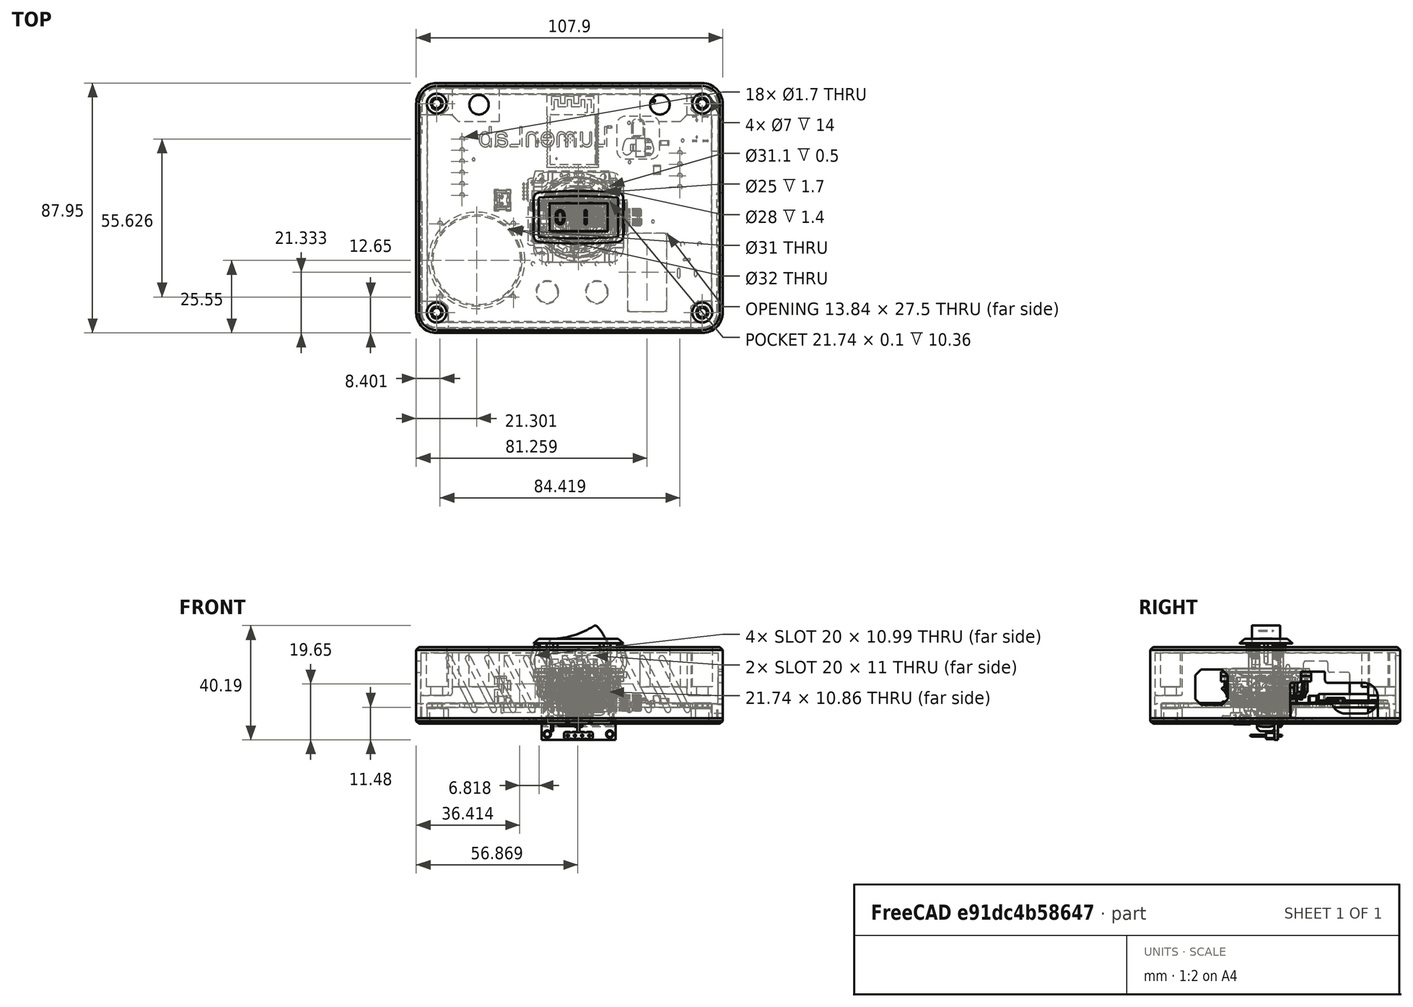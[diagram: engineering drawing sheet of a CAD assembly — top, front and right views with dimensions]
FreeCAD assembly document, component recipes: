
FREECAD ASSEMBLY — COMPONENT RECIPES ("lumenlab-enclosure")

This assembly document has 7 components, labeled P0..P6 below (a component is one placed body or linked part). 6 of them carry a construction recipe — the FreeCAD feature program that regenerates the part from scratch, quoted from this document or its linked companion documents; the rest are supplied as boundary geometry only. No exploded tour is included for this assembly.
COMPONENT P0 — geometry summary ("lumenlab-pcb001"; no construction recipe available for this part):
  bounding box: 106.5 x 80.0 x 42.6 mm
  tessellated surface: 422,423 triangles
  volume: 30416 mm^3 (8% of its bounding box)
COMPONENT P1 — recipe-attached ("lid", modeled in this document).
Construction recipe (the document's own serialized feature program — sketch geometry with constraints, then the solid features built on it; lengths are millimeters unless a unit is written):

FEATURE [PartDesign::SubShapeBinder] Binder
  BindCopyOnChange = 0
  BindMode = 0
  ClaimChildren = false
  Context = -> Body [Binder.]
  Fuse = false
  MakeFace = true
  OffsetFill = false
  OffsetIntersection = false
  OffsetJoinType = 0
  OffsetOpenResult = false
  PartialLoad = false
  Refine = true
  Relative = true
  Support = -> [Board_aaa008]
  _Version = 2
FEATURE [Sketcher::SketchObject] Sketch
  ArcFitTolerance = 1e-06
  AttachmentOffset = pos=(0,0,3.75) rot=(0,0,1;0rad)
  AttachmentSupport = -> [Binder]
  ExternalGeometry = -> [Binder]
  ExternalTypes = [0]
  FullyConstrained = true
  MakeInternals = false
  MapMode = 5
  Placement = pos=(0,0,-5.3502) rot=(1,0,0;3.14159rad)
  _ExternalGeoVersion = 0
  sketch-geometry (10):
    g0: LineSegment StartX=-57.1492 StartY=33.5464 StartZ=0 EndX=-57.1492 EndY=-39.9989 EndZ=0
    g1: LineSegment StartX=-49.9485 StartY=-47.1996 StartZ=0 EndX=43.5501 EndY=-47.1996 EndZ=0
    g2: LineSegment StartX=50.7508 StartY=-39.9989 StartZ=0 EndX=50.7508 EndY=33.5464 EndZ=0
    g3: LineSegment StartX=43.5501 StartY=40.7472 StartZ=0 EndX=-49.9485 EndY=40.7472 EndZ=0
    g4: ArcOfCircle CenterX=-49.9485 CenterY=33.5464 CenterZ=0 NormalX=0 NormalY=0 NormalZ=1 AngleXU=0 Radius=7.20071 StartAngle=1.5708 EndAngle=3.14159
    g5: ArcOfCircle CenterX=-49.9485 CenterY=-39.9989 CenterZ=0 NormalX=0 NormalY=0 NormalZ=1 AngleXU=0 Radius=7.20071 StartAngle=3.14159 EndAngle=4.71239
    g6: ArcOfCircle CenterX=43.5501 CenterY=-39.9989 CenterZ=0 NormalX=0 NormalY=0 NormalZ=1 AngleXU=0 Radius=7.20071 StartAngle=4.71239 EndAngle=6.28319
    g7: ArcOfCircle CenterX=43.5501 CenterY=33.5464 CenterZ=0 NormalX=0 NormalY=0 NormalZ=1 AngleXU=0 Radius=7.20071 StartAngle=1e-16 EndAngle=1.5708
    g8: GeomPoint [constr] X=-57.1492 Y=40.7472 Z=0
    g9: GeomPoint [constr] X=50.7508 Y=-47.1996 Z=0
  constraints (23):
    c: Tangent(g0,g4) = -1.5708
    c: Tangent(g0,g5) = -1.5708
    c: Tangent(g1,g5) = -1.5708
    c: Tangent(g1,g6) = -1.5708
    c: Tangent(g2,g6) = -1.5708
    c: Tangent(g2,g7) = -1.5708
    c: Tangent(g3,g7) = -1.5708
    c: Tangent(g3,g4) = -1.5708
    c: Vertical(g0)
    c: Vertical(g2)
    c: Horizontal(g1)
    c: Horizontal(g3)
    c: Equal(g4,g5)
    c: Equal(g5,g6)
    c: Equal(g6,g7)
    c: PointOnObject(g8,g0)
    c: PointOnObject(g8,g3)
    c: PointOnObject(g9,g1)
    c: PointOnObject(g9,g2)
    c: DistanceX(g0,g-5) = 4  'enclosure-width'
    c: Coincident(g4,g-4)
    c: Distance(g-7,g2) = 4
    c: Distance(g-9,g1) = 4
FEATURE [PartDesign::Pad] Pad
  Direction = (0,0,-1)
  Length = 2
  Length2 = 10
  Profile = -> Sketch
  ReferenceAxis = -> Sketch [N_Axis]
  Refine = true
  SideType = 0
  Suppressed = false
  Type = 0
  Type2 = 0
FEATURE [Sketcher::SketchObject] Sketch001
  ArcFitTolerance = 1e-06
  AttachmentSupport = -> [Pad]
  ExternalGeometry = -> [Binder]
  ExternalTypes = [0]
  FullyConstrained = true
  MakeInternals = false
  MapMode = 5
  Placement = pos=(0,0,-5.3502) rot=(0,0,1;0rad)
  _ExternalGeoVersion = 0
  sketch-geometry (20):
    g0: LineSegment StartX=-55.15 StartY=39.9996 StartZ=0 EndX=-55.15 EndY=-33.5498 EndZ=0
    g1: LineSegment StartX=-49.95 StartY=-38.7498 StartZ=0 EndX=43.551 EndY=-38.7498 EndZ=0
    g2: LineSegment StartX=48.751 StartY=-33.5498 StartZ=0 EndX=48.751 EndY=39.9996 EndZ=0
    g3: LineSegment StartX=43.551 StartY=45.1996 StartZ=0 EndX=-49.95 EndY=45.1996 EndZ=0
    g4: ArcOfCircle CenterX=-49.95 CenterY=39.9996 CenterZ=0 NormalX=0 NormalY=0 NormalZ=1 AngleXU=0 Radius=5.19999 StartAngle=1.5708 EndAngle=3.14159
    g5: ArcOfCircle CenterX=-49.95 CenterY=-33.5498 CenterZ=0 NormalX=0 NormalY=0 NormalZ=1 AngleXU=0 Radius=5.19999 StartAngle=3.14159 EndAngle=4.71239
    g6: ArcOfCircle CenterX=43.551 CenterY=-33.5498 CenterZ=0 NormalX=0 NormalY=0 NormalZ=1 AngleXU=0 Radius=5.19999 StartAngle=4.71239 EndAngle=6.28319
    g7: ArcOfCircle CenterX=43.551 CenterY=39.9996 CenterZ=0 NormalX=0 NormalY=0 NormalZ=1 AngleXU=0 Radius=5.19999 StartAngle=5e-16 EndAngle=1.5708
    g8: GeomPoint [constr] X=-55.15 Y=45.1996 Z=0
    g9: GeomPoint [constr] X=48.751 Y=-38.7498 Z=0
    g10: LineSegment StartX=-53.35 StartY=39.9996 StartZ=0 EndX=-53.35 EndY=-33.5498 EndZ=0
    g11: LineSegment StartX=-49.95 StartY=-36.9498 StartZ=0 EndX=43.551 EndY=-36.9498 EndZ=0
    g12: LineSegment StartX=46.951 StartY=-33.5498 StartZ=0 EndX=46.951 EndY=39.9996 EndZ=0
    g13: LineSegment StartX=43.551 StartY=43.3996 StartZ=0 EndX=-49.95 EndY=43.3996 EndZ=0
    g14: ArcOfCircle CenterX=-49.95 CenterY=39.9996 CenterZ=0 NormalX=0 NormalY=0 NormalZ=1 AngleXU=0 Radius=3.39999 StartAngle=1.5708 EndAngle=3.14159
    g15: ArcOfCircle CenterX=-49.95 CenterY=-33.5498 CenterZ=0 NormalX=0 NormalY=0 NormalZ=1 AngleXU=0 Radius=3.39999 StartAngle=3.14159 EndAngle=4.71239
    g16: ArcOfCircle CenterX=43.551 CenterY=-33.5498 CenterZ=0 NormalX=0 NormalY=0 NormalZ=1 AngleXU=0 Radius=3.39999 StartAngle=4.71239 EndAngle=6.28319
    g17: ArcOfCircle CenterX=43.551 CenterY=39.9996 CenterZ=0 NormalX=0 NormalY=0 NormalZ=1 AngleXU=0 Radius=3.39999 StartAngle=0 EndAngle=1.5708
    g18: GeomPoint [constr] X=-53.35 Y=43.3996 Z=0
    g19: GeomPoint [constr] X=46.951 Y=-36.9498 Z=0
  constraints (46):
    c: Tangent(g0,g4) = -1.5708
    c: Tangent(g0,g5) = -1.5708
    c: Tangent(g1,g5) = -1.5708
    c: Tangent(g1,g6) = -1.5708
    c: Tangent(g2,g6) = -1.5708
    c: Tangent(g2,g7) = -1.5708
    c: Tangent(g3,g7) = -1.5708
    c: Tangent(g3,g4) = -1.5708
    c: Vertical(g0)
    c: Vertical(g2)
    c: Horizontal(g1)
    c: Horizontal(g3)
    c: Equal(g4,g5)
    c: Equal(g5,g6)
    c: Equal(g6,g7)
    c: PointOnObject(g8,g0)
    c: PointOnObject(g8,g3)
    c: PointOnObject(g9,g1)
    c: PointOnObject(g9,g2)
    c: DistanceX(g0,g-5) = 2
    c: Coincident(g4,g-4)
    c: DistanceX(g-7,g2) = 2
    c: DistanceY(g1,g-9) = 2
    c: Tangent(g10,g14) = -1.5708
    c: Tangent(g10,g15) = -1.5708
    c: Tangent(g11,g15) = -1.5708
    c: Tangent(g11,g16) = -1.5708
    c: Tangent(g12,g16) = -1.5708
    c: Tangent(g12,g17) = -1.5708
    c: Tangent(g13,g17) = -1.5708
    c: Tangent(g13,g14) = -1.5708
    c: Vertical(g10)
    c: Vertical(g12)
    c: Horizontal(g11)
    c: Horizontal(g13)
    c: Equal(g14,g15)
    c: Equal(g15,g16)
    c: Equal(g16,g17)
    c: PointOnObject(g18,g10)
    c: PointOnObject(g18,g13)
    c: PointOnObject(g19,g11)
    c: PointOnObject(g19,g12)
    c: DistanceX(g10,g-5) = 0.2
    c: DistanceX(g-7,g12) = 0.2
    c: DistanceY(g11,g-9) = 0.2
    c: Coincident(g14,g4)
FEATURE [PartDesign::Pad] Pad001
  BaseFeature = -> Pad
  Direction = (0,0,1)
  Length = 5
  Length2 = 10
  Profile = -> Sketch001
  ReferenceAxis = -> Sketch001 [N_Axis]
  Refine = true
  SideType = 0
  Suppressed = false
  Type = 0
  Type2 = 0
FEATURE [Sketcher::SketchObject] Sketch002
  ArcFitTolerance = 1e-06
  ExternalGeometry = -> [Binder,Pad001]
  ExternalTypes = [0]
  FullyConstrained = true
  MakeInternals = false
  MapMode = 5
  Placement = pos=(0,0,-2) rot=(1,0,0;3.14159rad)
  _ExternalGeoVersion = 0
  sketch-geometry (10):
    g0: LineSegment StartX=-53.1492 StartY=29.5498 StartZ=0 EndX=-53.35 EndY=29.5498 EndZ=0
    g1: LineSegment StartX=-45.95 StartY=36.7473 StartZ=0 EndX=-45.95 EndY=36.9498 EndZ=0
    g2: LineSegment StartX=-45.95 StartY=36.9498 StartZ=0 EndX=-49.95 EndY=36.9498 EndZ=0
    g3: LineSegment StartX=-53.35 StartY=29.5498 StartZ=0 EndX=-53.35 EndY=33.5498 EndZ=0
    g4: ArcOfCircle CenterX=-49.95 CenterY=33.5498 CenterZ=0 NormalX=0 NormalY=0 NormalZ=1 AngleXU=0 Radius=3.39999 StartAngle=1.5708 EndAngle=3.14159
    g5: LineSegment StartX=-53.1492 StartY=29.5498 StartZ=0 EndX=-48.6466 EndY=29.5498 EndZ=0
    g6: ArcOfCircle CenterX=-48.6466 CenterY=30.4451 CenterZ=0 NormalX=0 NormalY=0 NormalZ=1 AngleXU=0 Radius=0.895293 StartAngle=4.71239 EndAngle=5.38086
    g7: LineSegment StartX=-48.0918 StartY=29.7425 StartZ=0 EndX=-46.138 EndY=31.2855 EndZ=0
    g8: ArcOfCircle CenterX=-46.4444 CenterY=31.6735 CenterZ=0 NormalX=0 NormalY=0 NormalZ=1 AngleXU=0 Radius=0.494368 StartAngle=5.38086 EndAngle=6.28319
    g9: LineSegment StartX=-45.95 StartY=31.6735 StartZ=0 EndX=-45.95 EndY=36.7473 EndZ=0
  constraints (24):
    c: PointOnObject(g0,g-8)
    c: Horizontal(g0)
    c: PointOnObject(g1,g-7)
    c: Vertical(g1)
    c: Coincident(g2,g1)
    c: Coincident(g2,g-9)
    c: Coincident(g3,g0)
    c: Coincident(g3,g-9)
    c: Coincident(g4,g2)
    c: Coincident(g4,g3)
    c: PointOnObject(g0,g-10)
    c: PointOnObject(g1,g-11)
    c: DistanceY(g3,g3) = 4
    c: DistanceX(g2,g2) = 4
    c: Equal(g4,g-9)
    c: Coincident(g0,g5)
    c: Tangent(g5,g6) = -1.5708
    c: Tangent(g6,g7) = -1.5708
    c: Tangent(g7,g8) = -1.5708
    c: Tangent(g8,g9) = -1.5708
    c: Vertical(g9)
    c: Coincident(g9,g1)
    c: Horizontal(g5)
    c: Block(g7)
FEATURE [PartDesign::Pad] Pad002
  BaseFeature = -> Pad001
  Direction = (0,-1e-16,-1)
  Length = 10
  Length2 = 10
  Profile = -> Sketch002
  ReferenceAxis = -> Sketch002 [N_Axis]
  Refine = true
  SideType = 0
  Suppressed = false
  Type = 2
  Type2 = 0
FEATURE [PartDesign::Plane] DatumPlane
  AttachmentOffset = pos=(0,0,0) rot=(1,0,0;1.5708rad)
  AttachmentSupport = -> [Pad002]
  Length = 122.591
  MapMode = 45
  Placement = pos=(-3.1995,3.22491,-2.8502) rot=(1,0,0;1.5708rad)
  ResizeMode = 0
  Width = 64.6902
  expr: .AttachmentOffset.Rotation.Pitch = 0
FEATURE [PartDesign::Plane] DatumPlane001
  AttachmentOffset = pos=(0,0,0) rot=(1,0,0;1.5708rad)
  AttachmentSupport = -> [Pad002]
  Length = 101.209
  MapMode = 45
  Placement = pos=(-3.1995,3.22491,-2.8502) rot=(0.57735,0.57735,0.57735;2.0944rad)
  ResizeMode = 0
  Width = 63.2625
FEATURE [PartDesign::Line] DatumLine
  AttacherType = Attacher::AttachEngineLine
  AttachmentSupport = -> [DatumPlane001,DatumPlane]
  Length = 20
  MapMode = 30
  Placement = pos=(-3.1995,3.22491,-2.8502) rot=(0,1,0;3.14159rad)
  ResizeMode = 0
FEATURE [PartDesign::Mirrored] Mirrored
  BaseFeature = -> Pad002
  MirrorPlane = -> DatumPlane
  Originals = -> [Pad002]
  Refine = true
  Suppressed = false
  TransformMode = 0
FEATURE [PartDesign::Mirrored] Mirrored001
  BaseFeature = -> Mirrored
  MirrorPlane = -> DatumPlane001
  Originals = -> [Pad002]
  Refine = true
  Suppressed = false
  TransformMode = 0
FEATURE [PartDesign::PolarPattern] PolarPattern
  Angle = 360
  Axis = -> DatumLine
  BaseFeature = -> Mirrored001
  Mode = 0
  Occurrences = 2
  Offset = 120
  Originals = -> [Pad002]
  Refine = true
  Reversed = true
  SpacingPattern = [0]
  Spacings = [-1]
  Suppressed = false
  TransformMode = 0
FEATURE [Sketcher::SketchObject] Sketch003
  ArcFitTolerance = 1e-06
  AttachmentSupport = -> [PolarPattern]
  ExternalTypes = [0]
  FullyConstrained = true
  MakeInternals = false
  MapMode = 5
  Placement = pos=(0,0,-2) rot=(0,0,1;0rad)
  _ExternalGeoVersion = 0
  sketch-geometry (1):
    g0: Circle CenterX=-49.95 CenterY=-33.5498 CenterZ=0 NormalX=0 NormalY=0 NormalZ=1 AngleXU=0 Radius=2.425
  constraints (2):
    c: Coincident(g0,g-3)
    c: Diameter(g0) = 4.85
FEATURE [PartDesign::Pocket] Pocket
  BaseFeature = -> PolarPattern
  Direction = (0,0,-1)
  Length = 4.35
  Length2 = 5
  Profile = -> Sketch003
  ReferenceAxis = -> Sketch003 [N_Axis]
  Refine = true
  SideType = 0
  Suppressed = false
  Type = 0
  Type2 = 0
FEATURE [PartDesign::Mirrored] Mirrored002
  BaseFeature = -> Pocket
  MirrorPlane = -> DatumPlane
  Originals = -> [Pocket]
  Refine = true
  Suppressed = false
  TransformMode = 0
FEATURE [PartDesign::Mirrored] Mirrored003
  BaseFeature = -> Mirrored002
  MirrorPlane = -> DatumPlane001
  Originals = -> [Pocket]
  Refine = true
  Suppressed = false
  TransformMode = 0
FEATURE [PartDesign::PolarPattern] PolarPattern001
  Angle = 360
  Axis = -> DatumLine
  BaseFeature = -> Mirrored003
  Mode = 0
  Occurrences = 2
  Offset = 120
  Originals = -> [Pocket]
  Refine = true
  SpacingPattern = [0]
  Spacings = [-1]
  Suppressed = false
  TransformMode = 0
FEATURE [Sketcher::SketchObject] Sketch004
  ArcFitTolerance = 1e-06
  AttachmentSupport = -> [Pad]
  ExternalTypes = [0]
  FullyConstrained = true
  MakeInternals = false
  MapMode = 5
  Placement = pos=(0,0,-5.3502) rot=(0,0,1;0rad)
  _ExternalGeoVersion = 0
  sketch-geometry (16):
    g0: LineSegment StartX=17.1876 StartY=-6.3741 StartZ=0 EndX=17.1876 EndY=-32.4599 EndZ=0
    g1: LineSegment StartX=17.8947 StartY=-33.167 StartZ=0 EndX=30.3239 EndY=-33.167 EndZ=0
    g2: LineSegment StartX=31.031 StartY=-32.4599 StartZ=0 EndX=31.031 EndY=-6.3741 EndZ=0
    g3: LineSegment StartX=30.3239 StartY=-5.66699 StartZ=0 EndX=17.8947 EndY=-5.66699 EndZ=0
    g4: ArcOfCircle [constr] CenterX=17.8947 CenterY=-6.3741 CenterZ=0 NormalX=0 NormalY=0 NormalZ=1 AngleXU=0 Radius=0.707107 StartAngle=1.5708 EndAngle=3.14159
    g5: GeomPoint [constr] X=17.1876 Y=-5.66699 Z=0
    g6: LineSegment StartX=17.8947 StartY=-5.66699 StartZ=0 EndX=17.1876 EndY=-6.3741 EndZ=0
    g7: ArcOfCircle [constr] CenterX=30.3239 CenterY=-6.3741 CenterZ=0 NormalX=0 NormalY=0 NormalZ=1 AngleXU=0 Radius=0.707107 StartAngle=-1.8e-15 EndAngle=1.5708
    g8: GeomPoint [constr] X=31.031 Y=-5.66699 Z=0
    g9: LineSegment StartX=31.031 StartY=-6.3741 StartZ=0 EndX=30.3239 EndY=-5.66699 EndZ=0
    g10: ArcOfCircle [constr] CenterX=30.3239 CenterY=-32.4599 CenterZ=0 NormalX=0 NormalY=0 NormalZ=1 AngleXU=0 Radius=0.707107 StartAngle=4.71239 EndAngle=6.28319
    g11: GeomPoint [constr] X=31.031 Y=-33.167 Z=0
    g12: LineSegment StartX=30.3239 StartY=-33.167 StartZ=0 EndX=31.031 EndY=-32.4599 EndZ=0
    g13: ArcOfCircle [constr] CenterX=17.8947 CenterY=-32.4599 CenterZ=0 NormalX=0 NormalY=0 NormalZ=1 AngleXU=0 Radius=0.707107 StartAngle=3.14159 EndAngle=4.71239
    g14: GeomPoint [constr] X=17.1876 Y=-33.167 Z=0
    g15: LineSegment StartX=17.1876 StartY=-32.4599 StartZ=0 EndX=17.8947 EndY=-33.167 EndZ=0
  constraints (36):
    c: Vertical(g0)
    c: Vertical(g2)
    c: Horizontal(g1)
    c: Distance(g14,g5) = 27.5
    c: Tangent(g0,g4) = -1.5708
    c: Tangent(g3,g4) = -1.5708
    c: Coincident(g6,g0)
    c: Coincident(g6,g3)
    c: Tangent(g2,g7) = -1.5708
    c: Tangent(g3,g7) = -1.5708
    c: Coincident(g9,g2)
    c: Coincident(g9,g3)
    c: PointOnObject(g11,g1)
    c: PointOnObject(g11,g2)
    c: Tangent(g1,g10) = -1.5708
    c: Tangent(g2,g10) = -1.5708
    c: Coincident(g12,g1)
    c: Coincident(g12,g2)
    c: PointOnObject(g14,g0)
    c: PointOnObject(g14,g1)
    c: Tangent(g0,g13) = -1.5708
    c: Tangent(g1,g13) = -1.5708
    c: Coincident(g15,g0)
    c: Coincident(g15,g1)
    c: DistanceX(g5,g-6) = 0.25
    c: Vertical(g5,g0)
    c: Horizontal(g3,g5)
    c: Horizontal(g-3,g3)
    c: Horizontal(g3)
    c: DistanceX(g8,g-6) = -0.25
    c: Vertical(g8,g2)
    c: Horizontal(g8,g3)
    c: Equal(g15,g12)
    c: Distance(g15,g15) = 1
    c: Equal(g15,g6)
    c: Equal(g15,g9)
FEATURE [PartDesign::Pocket] Pocket001
  BaseFeature = -> PolarPattern001
  Direction = (0,0,-1)
  Length = 5
  Length2 = 5
  Profile = -> Sketch004
  ReferenceAxis = -> Sketch004 [N_Axis]
  Refine = true
  SideType = 0
  Suppressed = false
  Type = 1
  Type2 = 0
FEATURE [Sketcher::SketchObject] Sketch005
  ArcFitTolerance = 1e-06
  AttachmentSupport = -> [Pocket001]
  ExternalGeometry = -> [Binder]
  ExternalTypes = [0]
  FullyConstrained = true
  MakeInternals = false
  MapMode = 5
  Placement = pos=(0,0,-5.3502) rot=(0,0,1;0rad)
  _ExternalGeoVersion = 0
  sketch-geometry (2):
    g0: Circle CenterX=-11.0304 CenterY=-26.366 CenterZ=0 NormalX=0 NormalY=0 NormalZ=1 AngleXU=0 Radius=4
    g1: Circle CenterX=6.40289 CenterY=-26.366 CenterZ=0 NormalX=0 NormalY=0 NormalZ=1 AngleXU=0 Radius=4
  constraints (4):
    c: Diameter(g1) = 8
    c: Diameter(g0) = 8
    c: Coincident(g0,g-3)
    c: Coincident(g1,g-4)
FEATURE [PartDesign::Pocket] Pocket002
  BaseFeature = -> Pocket001
  Direction = (0,0,-1)
  Length = 5
  Length2 = 5
  Profile = -> Sketch005
  ReferenceAxis = -> Sketch005 [N_Axis]
  Refine = true
  SideType = 0
  Suppressed = false
  Type = 1
  Type2 = 0
FEATURE [Sketcher::SketchObject] Sketch006
  ArcFitTolerance = 1e-06
  AttachmentSupport = -> [Pocket002]
  ExternalGeometry = -> [Binder]
  ExternalTypes = [0]
  FullyConstrained = true
  MakeInternals = false
  MapMode = 5
  Placement = pos=(0,0,-7.3502) rot=(1,0,0;3.14159rad)
  _ExternalGeoVersion = 0
  sketch-geometry (7):
    g0: GeomPoint [constr] X=-14.1384 Y=2.33766 Z=0
    g1: LineSegment StartX=-16.2684 StartY=8.33766 StartZ=0 EndX=-16.2684 EndY=-12.1623 EndZ=0
    g2: LineSegment StartX=-16.2684 StartY=-12.1623 StartZ=0 EndX=11.7316 EndY=-12.1623 EndZ=0
    g3: LineSegment StartX=11.7316 StartY=-12.1623 StartZ=0 EndX=11.7316 EndY=8.33766 EndZ=0
    g4: LineSegment StartX=11.7316 StartY=8.33766 StartZ=0 EndX=-16.2684 EndY=8.33766 EndZ=0
    g5: LineSegment [constr] StartX=-14.1384 StartY=2.33766 StartZ=0 EndX=-16.2684 EndY=8.33766 EndZ=0
    g6: LineSegment [constr] StartX=9.60158 StartY=2.33766 StartZ=0 EndX=11.7316 EndY=8.33766 EndZ=0
  constraints (17):
    c: Coincident(g0,g-4)
    c: Coincident(g1,g2)
    c: Coincident(g2,g3)
    c: Coincident(g3,g4)
    c: Coincident(g4,g1)
    c: Vertical(g1)
    c: Vertical(g3)
    c: Horizontal(g2)
    c: Horizontal(g4)
    c: Distance(g1,g3) = 28
    c: Distance(g2,g4) = 20.5
    c: Coincident(g5,g0)
    c: Coincident(g5,g1)
    c: Coincident(g6,g3)
    c: Coincident(g-3,g6)
    c: Equal(g5,g6)
    c: Distance(g2,g-5) = 1
FEATURE [PartDesign::Pocket] Pocket003
  BaseFeature = -> Pocket002
  Direction = (0,0,1)
  Length = 5
  Length2 = 5
  Profile = -> Sketch006
  ReferenceAxis = -> Sketch006 [N_Axis]
  Refine = true
  SideType = 0
  Suppressed = false
  Type = 1
  Type2 = 0
FEATURE [Sketcher::SketchObject] Sketch007
  ArcFitTolerance = 1e-06
  AttachmentSupport = -> [Pocket003]
  ExternalGeometry = -> [Binder]
  ExternalTypes = [0]
  FullyConstrained = true
  MakeInternals = false
  MapMode = 5
  Placement = pos=(0,0,-5.3502) rot=(0,0,1;0rad)
  _ExternalGeoVersion = 0
  sketch-geometry (1):
    g0: Circle CenterX=-35.849 CenterY=-15.2004 CenterZ=0 NormalX=0 NormalY=0 NormalZ=1 AngleXU=0 Radius=16
  constraints (2):
    c: Coincident(g0,g-3)
    c: Distance(g-3,g0) = 0.5
FEATURE [PartDesign::Pocket] Pocket004
  BaseFeature = -> Pocket003
  Direction = (0,0,-1)
  Length = 5
  Length2 = 5
  Profile = -> Sketch007
  ReferenceAxis = -> Sketch007 [N_Axis]
  Refine = true
  SideType = 0
  Suppressed = false
  Type = 1
  Type2 = 0
FEATURE [PartDesign::Chamfer] Chamfer
  Angle = 45
  Base = -> Pocket004 [Edge66]
  BaseFeature = -> Pocket004
  ChamferType = 0
  FlipDirection = false
  Refine = true
  Size = 1
  Size2 = 1
  SupportTransform = false
  Suppressed = false
  UseAllEdges = false
FEATURE [PartDesign::Chamfer] Chamfer001
  Angle = 45
  Base = -> Chamfer [Edge64]
  BaseFeature = -> Chamfer
  ChamferType = 0
  FlipDirection = false
  Refine = true
  Size = 1.5
  Size2 = 1
  SupportTransform = false
  Suppressed = false
  UseAllEdges = false
FEATURE [PartDesign::Chamfer] Chamfer002
  Angle = 45
  Base = -> Chamfer001 [Edge4]
  BaseFeature = -> Chamfer001
  ChamferType = 0
  FlipDirection = false
  Refine = true
  Size = 1.5
  Size2 = 1
  SupportTransform = false
  Suppressed = false
  UseAllEdges = false
FEATURE [PartDesign::Chamfer] Chamfer003
  Angle = 45
  Base = -> Chamfer002 [Edge7,Edge2]
  BaseFeature = -> Chamfer002
  ChamferType = 0
  FlipDirection = false
  Refine = true
  Size = 1.5
  Size2 = 1
  SupportTransform = false
  Suppressed = false
  UseAllEdges = false
FEATURE [Sketcher::SketchObject] Sketch008
  ArcFitTolerance = 1e-06
  AttachmentSupport = -> [Chamfer003]
  ExternalGeometry = -> [Chamfer003]
  ExternalTypes = [0]
  FullyConstrained = true
  MakeInternals = false
  MapMode = 5
  Placement = pos=(0,0,-5.3502) rot=(0,0,1;0rad)
  _ExternalGeoVersion = 0
  sketch-geometry (6):
    g0: LineSegment StartX=-15.2684 StartY=16.1623 StartZ=0 EndX=-16.2684 EndY=12.1623 EndZ=0
    g1: LineSegment StartX=-16.2684 StartY=12.1623 StartZ=0 EndX=11.7316 EndY=12.1623 EndZ=0
    g2: LineSegment StartX=11.7316 StartY=12.1623 StartZ=0 EndX=10.7316 EndY=16.1623 EndZ=0
    g3: LineSegment StartX=10.7316 StartY=16.1623 StartZ=0 EndX=-15.2684 EndY=16.1623 EndZ=0
    g4: LineSegment [constr] StartX=-15.2684 StartY=16.1623 StartZ=0 EndX=-17.7684 EndY=13.6623 EndZ=0
    g5: LineSegment [constr] StartX=13.2316 StartY=13.6623 StartZ=0 EndX=10.7316 EndY=16.1623 EndZ=0
  constraints (15):
    c: Coincident(g0,g1)
    c: Coincident(g1,g2)
    c: Coincident(g2,g3)
    c: Coincident(g3,g0)
    c: Horizontal(g3)
    c: Coincident(g5,g-3)
    c: Coincident(g4,g0)
    c: Coincident(g5,g2)
    c: Equal(g4,g5)
    c: Equal(g0,g2)
    c: Horizontal(g1)
    c: DistanceX(g0,g0) = 1
    c: Coincident(g0,g-5)
    c: Coincident(g-4,g4)
    c: DistanceY(g0,g0) = 4
FEATURE [PartDesign::Pocket] Pocket005
  BaseFeature = -> Chamfer003
  Direction = (0,0,-1)
  Length = 1
  Length2 = 5
  Profile = -> Sketch008
  ReferenceAxis = -> Sketch008 [N_Axis]
  Refine = true
  SideType = 0
  Suppressed = false
  Type = 0
  Type2 = 0
FEATURE [Sketcher::SketchObject] Sketch009
  ArcFitTolerance = 1e-06
  AttachmentSupport = -> [Pocket005]
  ExternalGeometry = -> [Pocket005]
  ExternalTypes = [0]
  FullyConstrained = true
  MakeInternals = false
  MapMode = 5
  Placement = pos=(0,0,-5.3502) rot=(0,0,1;0rad)
  _ExternalGeoVersion = 0
  sketch-geometry (6):
    g0: LineSegment StartX=-16.2684 StartY=-8.33766 StartZ=0 EndX=-14.7684 EndY=-12.3377 EndZ=0
    g1: LineSegment StartX=-14.7684 StartY=-12.3377 StartZ=0 EndX=10.2316 EndY=-12.3377 EndZ=0
    g2: LineSegment StartX=10.2316 StartY=-12.3377 StartZ=0 EndX=11.7316 EndY=-8.33766 EndZ=0
    g3: LineSegment StartX=11.7316 StartY=-8.33766 StartZ=0 EndX=-16.2684 EndY=-8.33766 EndZ=0
    g4: LineSegment [constr] StartX=-14.7684 StartY=-12.3377 StartZ=0 EndX=-17.7684 EndY=-9.83766 EndZ=0
    g5: LineSegment [constr] StartX=10.2316 StartY=-12.3377 StartZ=0 EndX=13.2316 EndY=-9.83766 EndZ=0
  constraints (15):
    c: Coincident(g0,g1)
    c: Coincident(g1,g2)
    c: Coincident(g2,g3)
    c: Horizontal(g1)
    c: Coincident(g4,g0)
    c: Coincident(g4,g-4)
    c: Coincident(g5,g1)
    c: Coincident(g5,g-5)
    c: Equal(g4,g5)
    c: Equal(g0,g2)
    c: Horizontal(g3)
    c: DistanceX(g0,g0) = 1.5
    c: DistanceY(g0,g0) = 4
    c: Coincident(g0,g3)
    c: Coincident(g0,g-6)
FEATURE [PartDesign::Pocket] Pocket006
  BaseFeature = -> Pocket005
  Direction = (0,0,-1)
  Length = 1
  Length2 = 5
  Profile = -> Sketch009
  ReferenceAxis = -> Sketch009 [N_Axis]
  Refine = true
  SideType = 0
  Suppressed = false
  Type = 0
  Type2 = 0
FEATURE [Sketcher::SketchObject] Sketch017
  ArcFitTolerance = 1e-06
  AttachmentSupport = -> [Pocket006]
  ExternalGeometry = -> [Binder,Pocket006]
  ExternalTypes = [0]
  FullyConstrained = true
  MakeInternals = false
  MapMode = 5
  Placement = pos=(-55.15,0,0) rot=(0.57735,-0.57735,-0.57735;2.0944rad)
  _ExternalGeoVersion = 0
  sketch-geometry (4):
    g0: LineSegment StartX=-29.4759 StartY=-0.350198 StartZ=0 EndX=-29.4759 EndY=-5.3502 EndZ=0
    g1: LineSegment StartX=-29.4759 StartY=-5.3502 StartZ=0 EndX=-5.57586 EndY=-5.3502 EndZ=0
    g2: LineSegment StartX=-5.57586 StartY=-5.3502 StartZ=0 EndX=-5.57586 EndY=-0.350198 EndZ=0
    g3: LineSegment StartX=-5.57586 StartY=-0.350198 StartZ=0 EndX=-29.4759 EndY=-0.350198 EndZ=0
  constraints (12):
    c: Coincident(g0,g1)
    c: Coincident(g1,g2)
    c: Coincident(g2,g3)
    c: Coincident(g3,g0)
    c: Vertical(g0)
    c: Vertical(g2)
    c: Horizontal(g1)
    c: PointOnObject(g1,g-5)
    c: Distance(g-3,g0) = 0.1
    c: Distance(g2,g-4) = 0.1
    c: DistanceY(g0,g0) = 5
    c: Equal(g0,g2)
FEATURE [PartDesign::Pad] Pad006
  BaseFeature = -> Pocket006
  Direction = (-1,0,0)
  Length = 2
  Length2 = 10
  Profile = -> Sketch017
  ReferenceAxis = -> Sketch017 [N_Axis]
  Refine = true
  SideType = 0
  Suppressed = false
  Type = 0
  Type2 = 0
FEATURE [PartDesign::Fillet] Fillet003
  Base = -> Pad006 [Edge224,Edge214]
  BaseFeature = -> Pad006
  Radius = 1
  Refine = true
  SupportTransform = false
  Suppressed = false
  UseAllEdges = false
FEATURE [Sketcher::SketchObject] Sketch018
  ArcFitTolerance = 1e-06
  AttachmentSupport = -> [Fillet003]
  ExternalGeometry = -> [Binder,Fillet003]
  ExternalTypes = [0]
  FullyConstrained = true
  MakeInternals = false
  MapMode = 5
  Placement = pos=(48.751,0,0) rot=(0.57735,0.57735,0.57735;2.0944rad)
  _ExternalGeoVersion = 0
  sketch-geometry (4):
    g0: LineSegment StartX=8.59847 StartY=-0.350198 StartZ=0 EndX=8.59847 EndY=-5.3502 EndZ=0
    g1: LineSegment StartX=8.59847 StartY=-5.3502 StartZ=0 EndX=39.3209 EndY=-5.3502 EndZ=0
    g2: LineSegment StartX=39.3209 StartY=-0.350198 StartZ=0 EndX=8.59847 EndY=-0.350198 EndZ=0
    g3: LineSegment StartX=39.3209 StartY=-5.3502 StartZ=0 EndX=39.3209 EndY=-0.350198 EndZ=0
  constraints (12):
    c: Coincident(g0,g1)
    c: Coincident(g2,g0)
    c: Vertical(g0)
    c: Horizontal(g1)
    c: Horizontal(g2)
    c: PointOnObject(g0,g-5)
    c: Distance(g0,g-3) = 0.1
    c: DistanceY(g0,g0) = 5
    c: Vertical(g3)
    c: Distance(g3,g-7) = 3.65
    c: Coincident(g1,g3)
    c: Coincident(g3,g2)
FEATURE [PartDesign::Pad] Pad007
  BaseFeature = -> Fillet003
  Direction = (1,0,0)
  Length = 2
  Length2 = 10
  Profile = -> Sketch018
  ReferenceAxis = -> Sketch018 [N_Axis]
  Refine = true
  SideType = 0
  Suppressed = false
  Type = 0
  Type2 = 0
FEATURE [Sketcher::SketchObject] Sketch019
  ArcFitTolerance = 1e-06
  AttachmentSupport = -> [Pad007]
  ExternalGeometry = -> [Binder]
  ExternalTypes = [0]
  FullyConstrained = true
  MakeInternals = false
  MapMode = 5
  Placement = pos=(48.751,0,0) rot=(0.57735,0.57735,0.57735;2.0944rad)
  _ExternalGeoVersion = 0
  sketch-geometry (10):
    g0: LineSegment StartX=22.9809 StartY=2.01 StartZ=0 EndX=22.9809 EndY=1.3 EndZ=0
    g1: LineSegment StartX=28.0309 StartY=-3.75 StartZ=0 EndX=34.3709 EndY=-3.75 EndZ=0
    g2: LineSegment StartX=39.4209 StartY=1.3 StartZ=0 EndX=39.4209 EndY=2.01 EndZ=0
    g3: LineSegment StartX=34.3709 StartY=7.06 StartZ=0 EndX=28.0309 EndY=7.06 EndZ=0
    g4: ArcOfCircle CenterX=28.0309 CenterY=2.01 CenterZ=0 NormalX=0 NormalY=0 NormalZ=1 AngleXU=0 Radius=5.05 StartAngle=1.5708 EndAngle=3.14159
    g5: ArcOfCircle CenterX=28.0309 CenterY=1.3 CenterZ=0 NormalX=0 NormalY=0 NormalZ=1 AngleXU=0 Radius=5.05 StartAngle=3.14159 EndAngle=4.71239
    g6: ArcOfCircle CenterX=34.3709 CenterY=1.3 CenterZ=0 NormalX=0 NormalY=0 NormalZ=1 AngleXU=0 Radius=5.05 StartAngle=4.71239 EndAngle=6.28319
    g7: ArcOfCircle CenterX=34.3709 CenterY=2.01 CenterZ=0 NormalX=0 NormalY=0 NormalZ=1 AngleXU=0 Radius=5.05 StartAngle=0 EndAngle=1.5708
    g8: GeomPoint [constr] X=22.9809 Y=7.06 Z=0
    g9: GeomPoint [constr] X=39.4209 Y=-3.75 Z=0
  constraints (21):
    c: Tangent(g0,g4) = -1.5708
    c: Tangent(g0,g5) = -1.5708
    c: Tangent(g1,g5) = -1.5708
    c: Tangent(g1,g6) = -1.5708
    c: Tangent(g2,g6) = -1.5708
    c: Tangent(g2,g7) = -1.5708
    c: Tangent(g3,g7) = -1.5708
    c: Tangent(g3,g4) = -1.5708
    c: Vertical(g0)
    c: Vertical(g2)
    c: Horizontal(g1)
    c: Horizontal(g3)
    c: Equal(g5,g6)
    c: PointOnObject(g8,g0)
    c: PointOnObject(g8,g3)
    c: PointOnObject(g9,g1)
    c: PointOnObject(g9,g2)
    c: Coincident(g4,g-4)
    c: Coincident(g5,g-10)
    c: Coincident(g7,g-6)
    c: DistanceX(g0,g-4) = 3.75
FEATURE [PartDesign::Body] Body  label="lid"
  AllowCompound = false
  Group = -> [Binder,Sketch,Pad,Sketch001,Pad001,Sketch002,Pad002,DatumPlane,Mirrored,DatumPlane001,Mirrored001,DatumLine,PolarPattern,Sketch003,Pocket,Mirrored002,Mirrored003,PolarPattern001,Sketch004,Pocket001,Sketch005,Pocket002,Sketch006,Pocket003,Sketch007,Pocket004,Chamfer,Chamfer001,Chamfer002,Chamfer003,Sketch008,Pocket005,Sketch009,Pocket006,Sketch017,Pad006,Fillet003,Sketch018,Pad007,Sketch019,+3 more]
  Origin = -> Origin032
  Tip = -> Fillet009
COMPONENT P2 — recipe-attached ("Body", modeled in this document).
Construction recipe (the document's own serialized feature program — sketch geometry with constraints, then the solid features built on it; lengths are millimeters unless a unit is written):

FEATURE [PartDesign::SubShapeBinder] Binder001
  BindCopyOnChange = 0
  BindMode = 0
  ClaimChildren = false
  Context = -> Body001 [Binder001.]
  Fuse = false
  MakeFace = true
  OffsetFill = false
  OffsetIntersection = false
  OffsetJoinType = 0
  OffsetOpenResult = false
  PartialLoad = false
  Refine = true
  Relative = true
  Support = -> [Board_aaa008]
  _Version = 2
FEATURE [Sketcher::SketchObject] Sketch010
  ArcFitTolerance = 1e-06
  AttachmentOffset = pos=(0,0,3.75) rot=(0,0,1;0rad)
  AttachmentSupport = -> [Binder001]
  ExternalGeometry = -> [Binder001]
  ExternalTypes = [0]
  FullyConstrained = true
  MakeInternals = false
  MapMode = 5
  Placement = pos=(0,0,-5.3502) rot=(1,0,0;3.14159rad)
  _ExternalGeoVersion = 0
  sketch-geometry (19):
    g0: LineSegment StartX=-57.1492 StartY=33.5464 StartZ=0 EndX=-57.1492 EndY=-39.9996 EndZ=0
    g1: LineSegment StartX=-49.9492 StartY=-47.1996 StartZ=0 EndX=43.5508 EndY=-47.1996 EndZ=0
    g2: LineSegment StartX=50.7508 StartY=-39.9996 StartZ=0 EndX=50.7508 EndY=33.5464 EndZ=0
    g3: LineSegment StartX=43.5508 StartY=40.7464 StartZ=0 EndX=-49.9492 EndY=40.7464 EndZ=0
    g4: ArcOfCircle CenterX=-49.9492 CenterY=33.5464 CenterZ=0 NormalX=0 NormalY=0 NormalZ=1 AngleXU=0 Radius=7.19996 StartAngle=1.5708 EndAngle=3.14159
    g5: ArcOfCircle CenterX=-49.9492 CenterY=-39.9996 CenterZ=0 NormalX=0 NormalY=0 NormalZ=1 AngleXU=0 Radius=7.19996 StartAngle=3.14159 EndAngle=4.71239
    g6: ArcOfCircle CenterX=43.5508 CenterY=-39.9996 CenterZ=0 NormalX=0 NormalY=0 NormalZ=1 AngleXU=0 Radius=7.19996 StartAngle=4.71239 EndAngle=6.28319
    g7: ArcOfCircle CenterX=43.5508 CenterY=33.5464 CenterZ=0 NormalX=0 NormalY=0 NormalZ=1 AngleXU=0 Radius=7.19996 StartAngle=0 EndAngle=1.5708
    g8: GeomPoint [constr] X=-57.1492 Y=40.7464 Z=0
    g9: GeomPoint [constr] X=50.7508 Y=-47.1996 Z=0
    g10: LineSegment StartX=-49.9492 StartY=-45.5996 StartZ=0 EndX=43.5508 EndY=-45.5996 EndZ=0
    g11: LineSegment StartX=49.1508 StartY=-39.9996 StartZ=0 EndX=49.1508 EndY=33.5464 EndZ=0
    g12: LineSegment StartX=43.5508 StartY=39.1464 StartZ=0 EndX=-49.9492 EndY=39.1464 EndZ=0
    g13: LineSegment StartX=-55.5492 StartY=33.5464 StartZ=0 EndX=-55.5492 EndY=-39.9996 EndZ=0
    g14: ArcOfCircle CenterX=-49.9492 CenterY=-39.9996 CenterZ=0 NormalX=0 NormalY=0 NormalZ=1 AngleXU=0 Radius=5.59996 StartAngle=3.14159 EndAngle=4.71239
    g15: ArcOfCircle CenterX=43.5508 CenterY=-39.9996 CenterZ=0 NormalX=0 NormalY=0 NormalZ=1 AngleXU=0 Radius=5.59996 StartAngle=4.71239 EndAngle=6.28319
    g16: ArcOfCircle CenterX=43.5508 CenterY=33.5464 CenterZ=0 NormalX=0 NormalY=0 NormalZ=1 AngleXU=0 Radius=5.59996 StartAngle=4e-16 EndAngle=1.5708
    g17: ArcOfCircle CenterX=-49.9492 CenterY=33.5464 CenterZ=0 NormalX=0 NormalY=0 NormalZ=1 AngleXU=0 Radius=5.59996 StartAngle=1.5708 EndAngle=3.14159
    g18: GeomPoint [constr] X=-55.5492 Y=-45.5996 Z=0
  constraints (43):
    c: Tangent(g0,g4) = -1.5708
    c: Tangent(g0,g5) = -1.5708
    c: Tangent(g1,g5) = -1.5708
    c: Tangent(g1,g6) = -1.5708
    c: Tangent(g2,g6) = -1.5708
    c: Tangent(g2,g7) = -1.5708
    c: Tangent(g3,g7) = -1.5708
    c: Tangent(g3,g4) = -1.5708
    c: Vertical(g0)
    c: Vertical(g2)
    c: Horizontal(g1)
    c: Horizontal(g3)
    c: Equal(g4,g5)
    c: Equal(g5,g6)
    c: Equal(g6,g7)
    c: PointOnObject(g8,g0)
    c: PointOnObject(g8,g3)
    c: PointOnObject(g9,g1)
    c: PointOnObject(g9,g2)
    c: Distance(g0,g-3) = 4
    c: Coincident(g-10,g4)
    c: Distance(g2,g-7) = 4
    c: Distance(g1,g-4) = 4
    c: Tangent(g10,g14) = -1.5708
    c: Tangent(g10,g15) = -1.5708
    c: Tangent(g11,g15) = -1.5708
    c: Tangent(g11,g16) = -1.5708
    c: Tangent(g12,g16) = -1.5708
    c: Tangent(g12,g17) = -1.5708
    c: Tangent(g13,g17) = -1.5708
    c: Tangent(g13,g14) = -1.5708
    c: Horizontal(g10)
    c: Horizontal(g12)
    c: Vertical(g11)
    c: Vertical(g13)
    c: Equal(g14,g15)
    c: Equal(g15,g16)
    c: Equal(g16,g17)
    c: PointOnObject(g18,g10)
    c: PointOnObject(g18,g13)
    c: Distance(g0,g13) = 1.6
    c: Coincident(g14,g5)
    c: Coincident(g16,g7)
FEATURE [PartDesign::Pad] Pad003
  Direction = (0,0,-1)
  Length = 23
  Length2 = 10
  Profile = -> Sketch010
  ReferenceAxis = -> Sketch010 [N_Axis]
  Refine = true
  Reversed = true
  SideType = 0
  Suppressed = false
  Type = 0
  Type2 = 0
FEATURE [Sketcher::SketchObject] Sketch011
  ArcFitTolerance = 1e-06
  AttachmentSupport = -> [Pad003]
  ExternalGeometry = -> [Pad003]
  ExternalTypes = [0]
  FullyConstrained = true
  MakeInternals = false
  MapMode = 5
  Placement = pos=(0,0,17.6498) rot=(0,0,1;0rad)
  _ExternalGeoVersion = 0
  sketch-geometry (10):
    g0: LineSegment StartX=-57.1492 StartY=39.9996 StartZ=0 EndX=-57.1492 EndY=-33.5464 EndZ=0
    g1: LineSegment StartX=-49.9492 StartY=-40.7464 StartZ=0 EndX=43.5508 EndY=-40.7464 EndZ=0
    g2: LineSegment StartX=50.7508 StartY=-33.5464 StartZ=0 EndX=50.7508 EndY=39.9996 EndZ=0
    g3: LineSegment StartX=43.5508 StartY=47.1996 StartZ=0 EndX=-49.9492 EndY=47.1996 EndZ=0
    g4: ArcOfCircle CenterX=-49.9492 CenterY=39.9996 CenterZ=0 NormalX=0 NormalY=0 NormalZ=1 AngleXU=0 Radius=7.19996 StartAngle=1.5708 EndAngle=3.14159
    g5: ArcOfCircle CenterX=-49.9492 CenterY=-33.5464 CenterZ=0 NormalX=0 NormalY=0 NormalZ=1 AngleXU=0 Radius=7.19996 StartAngle=3.14159 EndAngle=4.71239
    g6: ArcOfCircle CenterX=43.5508 CenterY=-33.5464 CenterZ=0 NormalX=0 NormalY=0 NormalZ=1 AngleXU=0 Radius=7.19996 StartAngle=4.71239 EndAngle=6.28319
    g7: ArcOfCircle CenterX=43.5508 CenterY=39.9996 CenterZ=0 NormalX=0 NormalY=0 NormalZ=1 AngleXU=0 Radius=7.19996 StartAngle=0 EndAngle=1.5708
    g8: GeomPoint [constr] X=-57.1492 Y=47.1996 Z=0
    g9: GeomPoint [constr] X=50.7508 Y=-40.7464 Z=0
  constraints (20):
    c: Tangent(g0,g4) = -1.5708
    c: Tangent(g0,g5) = -1.5708
    c: Tangent(g1,g5) = -1.5708
    c: Tangent(g1,g6) = -1.5708
    c: Tangent(g2,g6) = -1.5708
    c: Tangent(g2,g7) = -1.5708
    c: Tangent(g3,g7) = -1.5708
    c: Tangent(g3,g4) = -1.5708
    c: Vertical(g2)
    c: Horizontal(g1)
    c: Equal(g4,g5)
    c: Equal(g5,g6)
    c: PointOnObject(g8,g0)
    c: PointOnObject(g8,g3)
    c: PointOnObject(g9,g1)
    c: PointOnObject(g9,g2)
    c: Coincident(g-5,g0)
    c: Coincident(g3,g-4)
    c: Coincident(g3,g-6)
    c: Coincident(g1,g-9)
FEATURE [PartDesign::Pad] Pad004
  BaseFeature = -> Pad003
  Direction = (0,0,1)
  Length = 2
  Length2 = 10
  Profile = -> Sketch011
  ReferenceAxis = -> Sketch011 [N_Axis]
  Refine = true
  SideType = 0
  Suppressed = false
  Type = 0
  Type2 = 0
FEATURE [Sketcher::SketchObject] Sketch012
  ArcFitTolerance = 1e-06
  AttachmentSupport = -> [Pad003]
  ExternalGeometry = -> [Binder001,Pad003]
  ExternalTypes = [0]
  FullyConstrained = true
  MakeInternals = false
  MapMode = 5
  Placement = pos=(-57.1492,0,0) rot=(0.57735,-0.57735,-0.57735;2.0944rad)
  _ExternalGeoVersion = 0
  sketch-geometry (10):
    g0: LineSegment StartX=-29.5259 StartY=10.75 StartZ=0 EndX=-29.5259 EndY=-5.3502 EndZ=0
    g1: LineSegment StartX=-5.52586 StartY=-5.3502 StartZ=0 EndX=-5.52586 EndY=10.75 EndZ=0
    g2: LineSegment StartX=-5.52586 StartY=10.75 StartZ=0 EndX=-13.2759 EndY=10.75 EndZ=0
    g3: LineSegment StartX=-29.5259 StartY=-5.3502 StartZ=0 EndX=-5.52586 EndY=-5.3502 EndZ=0
    g4: LineSegment StartX=-21.7759 StartY=10.75 StartZ=0 EndX=-21.7759 EndY=14.75 EndZ=0
    g5: LineSegment StartX=-21.7759 StartY=14.75 StartZ=0 EndX=-13.2759 EndY=14.75 EndZ=0
    g6: LineSegment StartX=-13.2759 StartY=14.75 StartZ=0 EndX=-13.2759 EndY=10.75 EndZ=0
    g7: LineSegment [constr] StartX=-21.7759 StartY=14.75 StartZ=0 EndX=-29.5259 EndY=10.75 EndZ=0
    g8: LineSegment [constr] StartX=-13.2759 StartY=14.75 StartZ=0 EndX=-5.52586 EndY=10.75 EndZ=0
    g9: LineSegment StartX=-21.7759 StartY=10.75 StartZ=0 EndX=-29.5259 EndY=10.75 EndZ=0
  constraints (29):
    c: Coincident(g1,g2)
    c: Coincident(g9,g0)
    c: Vertical(g0)
    c: Vertical(g1)
    c: Horizontal(g2)
    c: Distance(g-4,g1) = 0.15
    c: Distance(g-5,g2) = 2.25
    c: PointOnObject(g0,g-6)
    c: PointOnObject(g1,g-6)
    c: Coincident(g3,g0)
    c: Coincident(g3,g1)
    c: Distance(g-3,g0) = 0.15
    c: PointOnObject(g4,g9)
    c: Coincident(g4,g5)
    c: Horizontal(g5)
    c: Coincident(g5,g6)
    c: DistanceX(g5,g5) = 8.5
    c: Equal(g4,g6)
    c: Distance(g2,g5) = 4
    c: Vertical(g4)
    c: Coincident(g7,g4)
    c: Coincident(g7,g0)
    c: Coincident(g8,g5)
    c: Coincident(g8,g1)
    c: Equal(g7,g8)
    c: Coincident(g2,g6)
    c: PointOnObject(g9,g4)
    c: Horizontal(g9)
    c: Vertical(g6)
FEATURE [PartDesign::Pocket] Pocket007
  BaseFeature = -> Pad004
  Direction = (1,0,0)
  Length = 5
  Length2 = 5
  Profile = -> Sketch012
  ReferenceAxis = -> Sketch012 [N_Axis]
  Refine = true
  SideType = 0
  Suppressed = false
  Type = 2
  Type2 = 0
FEATURE [PartDesign::Fillet] Fillet
  Base = -> Pocket007 [Edge44,Edge46,Edge49,Edge51,Edge53,Edge54]
  BaseFeature = -> Pocket007
  Radius = 0.75
  Refine = true
  SupportTransform = false
  Suppressed = false
  UseAllEdges = false
FEATURE [PartDesign::Fillet] Fillet001
  Base = -> Fillet [Edge33,Edge20]
  BaseFeature = -> Fillet
  Radius = 1
  Refine = true
  SupportTransform = false
  Suppressed = false
  UseAllEdges = false
FEATURE [Sketcher::SketchObject] Sketch013
  ArcFitTolerance = 1e-06
  AttachmentSupport = -> [Fillet001]
  ExternalGeometry = -> [Binder001,Fillet001]
  ExternalTypes = [0]
  FullyConstrained = true
  MakeInternals = false
  MapMode = 5
  Placement = pos=(50.7508,0,3.061e-13) rot=(0.57735,0.57735,0.57735;2.0944rad)
  _ExternalGeoVersion = 0
  sketch-geometry (12):
    g0: LineSegment StartX=8.54847 StartY=7.05 StartZ=0 EndX=8.54847 EndY=-5.3502 EndZ=0
    g1: LineSegment StartX=24.4785 StartY=7.05 StartZ=0 EndX=20.7635 EndY=7.05 EndZ=0
    g2: LineSegment StartX=24.4785 StartY=7.05 StartZ=0 EndX=34.3709 EndY=7.05 EndZ=0
    g3: ArcOfCircle CenterX=34.3709 CenterY=2.01 CenterZ=0 NormalX=0 NormalY=0 NormalZ=1 AngleXU=0 Radius=5.04 StartAngle=0 EndAngle=1.5708
    g4: LineSegment StartX=39.4109 StartY=2.01 StartZ=0 EndX=39.4109 EndY=-5.3502 EndZ=0
    g5: LineSegment StartX=39.4109 StartY=-5.3502 StartZ=0 EndX=8.54847 EndY=-5.3502 EndZ=0
    g6: LineSegment StartX=12.2635 StartY=7.05 StartZ=0 EndX=12.2635 EndY=11.05 EndZ=0
    g7: LineSegment StartX=12.2635 StartY=11.05 StartZ=0 EndX=20.7635 EndY=11.05 EndZ=0
    g8: LineSegment StartX=20.7635 StartY=11.05 StartZ=0 EndX=20.7635 EndY=7.05 EndZ=0
    g9: LineSegment [constr] StartX=12.2635 StartY=11.05 StartZ=0 EndX=8.54847 EndY=7.05 EndZ=0
    g10: LineSegment [constr] StartX=24.4785 StartY=7.05 StartZ=0 EndX=20.7635 EndY=11.05 EndZ=0
    g11: LineSegment StartX=12.2635 StartY=7.05 StartZ=0 EndX=8.54847 EndY=7.05 EndZ=0
  constraints (34):
    c: Coincident(g11,g0)
    c: Vertical(g0)
    c: Horizontal(g1)
    c: Distance(g-5,g1) = 0.25
    c: Horizontal(g2)
    c: Tangent(g2,g3) = 1.5708
    c: Coincident(g3,g4)
    c: Vertical(g4)
    c: Coincident(g4,g5)
    c: Horizontal(g-11,g3)
    c: Coincident(g3,g-11)
    c: PointOnObject(g0,g-13)
    c: Horizontal(g5)
    c: PointOnObject(g6,g11)
    c: Coincident(g7,g6)
    c: Horizontal(g7)
    c: Coincident(g8,g7)
    c: Distance(g7,g1) = 4
    c: Coincident(g9,g6)
    c: Coincident(g9,g0)
    c: Coincident(g10,g7)
    c: Equal(g9,g10)
    c: Equal(g6,g8)
    c: Vertical(g6)
    c: DistanceX(g7,g7) = 8.5
    c: Coincident(g1,g8)
    c: PointOnObject(g11,g6)
    c: Vertical(g8)
    c: Horizontal(g11)
    c: Distance(g-5,g0) = 0.15
    c: Coincident(g1,g2)
    c: Vertical(g1,g-3)
    c: Coincident(g10,g1)
    c: Coincident(g5,g0)
FEATURE [PartDesign::Pocket] Pocket008
  BaseFeature = -> Fillet001
  Direction = (-1,-1e-16,-5.9e-15)
  Length = 5
  Length2 = 5
  Profile = -> Sketch013
  ReferenceAxis = -> Sketch013 [N_Axis]
  Refine = true
  SideType = 0
  Suppressed = false
  Type = 2
  Type2 = 0
FEATURE [Sketcher::SketchObject] Sketch014
  ArcFitTolerance = 1e-06
  ExternalGeometry = -> [Binder001]
  ExternalTypes = [0]
  FullyConstrained = true
  MakeInternals = false
  MapMode = 5
  Placement = pos=(50.7508,0,2.944e-13) rot=(0.57735,0.57735,0.57735;2.0944rad)
  _ExternalGeoVersion = 0
  sketch-geometry (4):
    g0: LineSegment StartX=-24.8504 StartY=11.7 StartZ=0 EndX=-24.8504 EndY=-0.7 EndZ=0
    g1: LineSegment StartX=-24.8504 StartY=-0.7 StartZ=0 EndX=-13.4504 EndY=-0.7 EndZ=0
    g2: LineSegment StartX=-13.4504 StartY=-0.7 StartZ=0 EndX=-13.4504 EndY=11.7 EndZ=0
    g3: LineSegment StartX=-13.4504 StartY=11.7 StartZ=0 EndX=-24.8504 EndY=11.7 EndZ=0
  constraints (12):
    c: Coincident(g0,g1)
    c: Coincident(g1,g2)
    c: Coincident(g2,g3)
    c: Coincident(g3,g0)
    c: Vertical(g0)
    c: Vertical(g2)
    c: Horizontal(g1)
    c: Horizontal(g3)
    c: Distance(g-5,g0) = 1
    c: Distance(g-6,g2) = 2
    c: Distance(g3,g-5) = 1
    c: Distance(g-4,g1) = 1
FEATURE [PartDesign::Pocket] Pocket009
  BaseFeature = -> Pocket008
  Direction = (-1,0,-5.8e-15)
  Length = 5
  Length2 = 5
  Profile = -> Sketch014
  ReferenceAxis = -> Sketch014 [N_Axis]
  Refine = true
  SideType = 0
  Suppressed = false
  Type = 2
  Type2 = 0
FEATURE [PartDesign::Chamfer] Chamfer004
  Angle = 45
  Base = -> Pocket009 [Edge135,Edge134,Edge133,Edge132]
  BaseFeature = -> Pocket009
  ChamferType = 0
  FlipDirection = false
  Refine = true
  Size = 2
  Size2 = 1
  SupportTransform = false
  Suppressed = false
  UseAllEdges = false
FEATURE [Sketcher::SketchObject] Sketch015
  ArcFitTolerance = 1e-06
  AttachmentSupport = -> [Chamfer004]
  ExternalGeometry = -> [Binder001,Chamfer004]
  ExternalTypes = [0]
  FullyConstrained = true
  MakeInternals = false
  MapMode = 5
  Placement = pos=(0,0,17.6498) rot=(1,0,0;3.14159rad)
  _ExternalGeoVersion = 0
  sketch-geometry (32):
    g0: LineSegment StartX=-55.5492 StartY=29.5464 StartZ=0 EndX=-49.9492 EndY=29.5464 EndZ=0
    g1: ArcOfCircle CenterX=-49.9492 CenterY=33.5464 CenterZ=0 NormalX=0 NormalY=0 NormalZ=1 AngleXU=0 Radius=4 StartAngle=4.71239 EndAngle=6.28319
    g2: LineSegment StartX=-45.9492 StartY=33.5464 StartZ=0 EndX=-45.9492 EndY=39.1464 EndZ=0
    g3: LineSegment StartX=-45.9492 StartY=39.1464 StartZ=0 EndX=-49.9492 EndY=39.1464 EndZ=0
    g4: ArcOfCircle CenterX=-49.9492 CenterY=33.5464 CenterZ=0 NormalX=0 NormalY=0 NormalZ=1 AngleXU=0 Radius=5.59996 StartAngle=1.5708 EndAngle=3.14159
    g5: LineSegment StartX=-55.5492 StartY=33.5464 StartZ=0 EndX=-55.5492 EndY=29.5464 EndZ=0
    g6: Circle CenterX=-49.9492 CenterY=33.5464 CenterZ=0 NormalX=0 NormalY=0 NormalZ=1 AngleXU=0 Radius=2
    g7: Circle CenterX=-49.9492 CenterY=-39.9996 CenterZ=0 NormalX=0 NormalY=0 NormalZ=1 AngleXU=0 Radius=2
    g8: LineSegment StartX=-27.9492 StartY=-45.5996 StartZ=0 EndX=-27.9492 EndY=-33.5996 EndZ=0
    g9: LineSegment StartX=-44.5492 StartY=-35.9996 StartZ=0 EndX=-55.5492 EndY=-35.9996 EndZ=0
    g10: LineSegment [constr] StartX=-55.5492 StartY=-39.9996 StartZ=0 EndX=-55.5492 EndY=-4.52586 EndZ=0
    g11: LineSegment StartX=-55.5492 StartY=-35.9996 StartZ=0 EndX=-55.5492 EndY=-39.9996 EndZ=0
    g12: ArcOfCircle CenterX=-49.9492 CenterY=-39.9996 CenterZ=0 NormalX=0 NormalY=0 NormalZ=1 AngleXU=0 Radius=5.59996 StartAngle=3.14159 EndAngle=4.71239
    g13: LineSegment StartX=-49.9492 StartY=-45.5996 StartZ=0 EndX=-27.9492 EndY=-45.5996 EndZ=0
    g14: LineSegment [constr] StartX=49.1508 StartY=-39.9996 StartZ=0 EndX=49.1508 EndY=-8.54847 EndZ=0
    g15: LineSegment StartX=43.5508 StartY=-45.5996 StartZ=0 EndX=21.551 EndY=-45.5996 EndZ=0
    g16: LineSegment StartX=21.551 StartY=-45.5996 StartZ=0 EndX=21.551 EndY=-33.5996 EndZ=0
    g17: LineSegment StartX=38.1508 StartY=-35.9996 StartZ=0 EndX=49.1508 EndY=-35.9996 EndZ=0
    g18: LineSegment StartX=49.1508 StartY=-35.9996 StartZ=0 EndX=49.1508 EndY=-39.9996 EndZ=0
    g19: ArcOfCircle CenterX=43.5508 CenterY=-39.9996 CenterZ=0 NormalX=0 NormalY=0 NormalZ=1 AngleXU=0 Radius=5.59996 StartAngle=4.71239 EndAngle=6.28319
    g20: Circle CenterX=43.551 CenterY=-39.9996 CenterZ=0 NormalX=0 NormalY=0 NormalZ=1 AngleXU=0 Radius=2
    g21: Circle CenterX=43.5508 CenterY=33.5498 CenterZ=0 NormalX=0 NormalY=0 NormalZ=1 AngleXU=0 Radius=2
    g22: LineSegment StartX=39.5508 StartY=39.1464 StartZ=0 EndX=39.5508 EndY=33.5498 EndZ=0
    g23: ArcOfCircle CenterX=43.5508 CenterY=33.5498 CenterZ=0 NormalX=0 NormalY=0 NormalZ=1 AngleXU=0 Radius=4 StartAngle=3.14158 EndAngle=4.7124
    g24: LineSegment StartX=43.5508 StartY=29.5498 StartZ=0 EndX=49.1508 EndY=29.5498 EndZ=0
    g25: LineSegment StartX=49.1508 StartY=29.5498 StartZ=0 EndX=49.1508 EndY=33.5464 EndZ=0
    g26: ArcOfCircle CenterX=43.5508 CenterY=33.5464 CenterZ=0 NormalX=0 NormalY=0 NormalZ=1 AngleXU=0 Radius=5.59996 StartAngle=0 EndAngle=1.5708
    g27: LineSegment StartX=39.5508 StartY=39.1464 StartZ=0 EndX=43.5508 EndY=39.1464 EndZ=0
    g28: LineSegment StartX=-27.9492 StartY=-33.5996 StartZ=0 EndX=-42.1491 EndY=-33.5996 EndZ=0
    g29: LineSegment StartX=-42.1491 StartY=-33.5996 StartZ=0 EndX=-44.5492 EndY=-35.9996 EndZ=0
    g30: LineSegment StartX=38.1508 StartY=-35.9996 StartZ=0 EndX=35.7508 EndY=-33.5996 EndZ=0
    g31: LineSegment StartX=35.7508 StartY=-33.5996 StartZ=0 EndX=21.551 EndY=-33.5996 EndZ=0
  constraints (80):
    c: PointOnObject(g0,g-7)
    c: Horizontal(g0)
    c: Tangent(g0,g1) = -1.5708
    c: Coincident(g1,g2)
    c: Vertical(g2)
    c: Coincident(g2,g3)
    c: Coincident(g3,g-9)
    c: Tangent(g3,g4) = -1.5708
    c: Coincident(g4,g-8)
    c: Tangent(g4,g5) = -1.5708
    c: Coincident(g6,g4)
    c: Coincident(g1,g4)
    c: DistanceY(g0,g1) = 4
    c: Coincident(g7,g-14)
    c: PointOnObject(g8,g-13)
    c: Vertical(g8)
    c: Horizontal(g9)
    c: Coincident(g10,g-14)
    c: Coincident(g10,g-7)
    c: Coincident(g9,g11)
    c: Coincident(g11,g10)
    c: Tangent(g11,g12) = -1.5708
    c: Coincident(g12,g-14)
    c: Tangent(g12,g13) = -1.5708
    c: DistanceY(g12,g9) = 4
    c: DistanceX(g12,g8) = 22
    c: Coincident(g13,g8)
    c: Coincident(g5,g0)
    c: Coincident(g14,g-11)
    c: Coincident(g14,g-12)
    c: Coincident(g-13,g15)
    c: PointOnObject(g15,g-13)
    c: Coincident(g15,g16)
    c: Vertical(g16)
    c: Horizontal(g17)
    c: Coincident(g17,g18)
    c: Tangent(g18,g19) = 1.5708
    c: Coincident(g19,g15)
    c: Coincident(g18,g14)
    c: PointOnObject(g17,g14)
    c: Coincident(g23,g24)
    c: DistanceY(g23,g21) = 4
    c: DistanceX(g22,g21) = 4
    c: Coincident(g26,g25)
    c: Coincident(g25,g-11)
    c: Coincident(g26,g-10)
    c: Coincident(g26,g27)
    c: Horizontal(g27)
    c: PointOnObject(g22,g-9)
    c: Coincident(g27,g22)
    c: Coincident(g23,g-4)
    c: Horizontal(g24)
    c: PointOnObject(g24,g-11)
    c: Coincident(g24,g25)
    c: Coincident(g22,g23)
    c: Vertical(g22)
    c: Coincident(g21,g23)
    c: Vertical(g23,g26)
    c: Coincident(g8,g28)
    c: Horizontal(g28)
    c: Coincident(g28,g29)
    c: Coincident(g29,g9)
    c: Angle(g9,g29,g9) = 0.785398
    c: DistanceY(g8,g8) = 12
    c: DistanceX(g9,g9) = 11
    c: DistanceY(g16,g16) = 12
    c: DistanceX(g17,g17) = 11
    c: Coincident(g30,g17)
    c: Coincident(g31,g30)
    c: Horizontal(g31)
    c: Angle(g17,g30,g17) = 2.35619
    c: Coincident(g31,g16)
    c: Coincident(g20,g-5)
    c: Distance(g20,g16) = 22
    c: Distance(g20,g17) = 4
    c: Diameter(g6) = 4
    c: Equal(g6,g7)
    c: Equal(g6,g21)
    c: Equal(g6,g20)
    c: Horizontal(g1,g1)
FEATURE [PartDesign::Pad] Pad005
  BaseFeature = -> Chamfer004
  Direction = (0,0,-1)
  Length = 15
  Length2 = 10
  Profile = -> Sketch015
  ReferenceAxis = -> Sketch015 [N_Axis]
  Refine = true
  SideType = 0
  Suppressed = false
  Type = 0
  Type2 = 0
FEATURE [Sketcher::SketchObject] Sketch016
  ArcFitTolerance = 1e-06
  AttachmentOffset = pos=(0,0,-2) rot=(0,0,1;0rad)
  AttachmentSupport = -> [Pad005]
  ExternalGeometry = -> [Pad005]
  ExternalTypes = [0]
  FullyConstrained = true
  MakeInternals = false
  MapMode = 5
  Placement = pos=(0,0,19.6498) rot=(1,0,0;3.14159rad)
  _ExternalGeoVersion = 0
  sketch-geometry (6):
    g0: Circle CenterX=-49.9492 CenterY=33.5464 CenterZ=0 NormalX=0 NormalY=0 NormalZ=1 AngleXU=0 Radius=3.5
    g1: Circle CenterX=43.5508 CenterY=33.5498 CenterZ=0 NormalX=0 NormalY=0 NormalZ=1 AngleXU=0 Radius=3.5
    g2: Circle CenterX=43.551 CenterY=-39.9996 CenterZ=0 NormalX=0 NormalY=0 NormalZ=1 AngleXU=0 Radius=3.5
    g3: Circle CenterX=-49.9492 CenterY=-39.9996 CenterZ=0 NormalX=0 NormalY=0 NormalZ=1 AngleXU=0 Radius=3.5
    g4: Circle CenterX=28.6509 CenterY=-39.5996 CenterZ=0 NormalX=0 NormalY=0 NormalZ=1 AngleXU=0 Radius=3.425
    g5: Circle CenterX=-35.0492 CenterY=-39.5996 CenterZ=0 NormalX=0 NormalY=0 NormalZ=1 AngleXU=0 Radius=3.425
  constraints (12):
    c: Coincident(g0,g-3)
    c: Coincident(g1,g-4)
    c: Coincident(g2,g-5)
    c: Coincident(g3,g-6)
    c: Radius(g0) = 3.5
    c: Equal(g0,g1)
    c: Equal(g0,g2)
    c: Equal(g0,g3)
    c: Diameter(g4) = 6.85
    c: Diameter(g5) = 6.85
    c: Symmetric(g-8,g-7,g5)
    c: Symmetric(g-9,g-10,g4)
FEATURE [PartDesign::Pocket] Pocket010
  BaseFeature = -> Pad005
  Direction = (0,0,1)
  Length = 14
  Length2 = 5
  Profile = -> Sketch016
  ReferenceAxis = -> Sketch016 [N_Axis]
  Refine = true
  Reversed = true
  SideType = 0
  Suppressed = false
  Type = 0
  Type2 = 0
FEATURE [PartDesign::Fillet] Fillet004
  Base = -> Pocket010 [Edge204,Edge105]
  BaseFeature = -> Pocket010
  Radius = 1
  Refine = true
  SupportTransform = false
  Suppressed = false
  UseAllEdges = false
FEATURE [PartDesign::Fillet] Fillet005
  Base = -> Fillet004 [Edge38,Edge67,Edge33]
  BaseFeature = -> Fillet004
  Radius = 0.5
  Refine = true
  SupportTransform = false
  Suppressed = false
  UseAllEdges = false
FEATURE [PartDesign::Chamfer] Chamfer005
  Angle = 45
  Base = -> Fillet005 [Edge15,Edge71,Edge70,Edge68,Edge66,Edge67,Edge69,Edge62]
  BaseFeature = -> Fillet005
  ChamferType = 0
  FlipDirection = false
  Refine = true
  Size = 1
  Size2 = 1
  SupportTransform = false
  Suppressed = false
  UseAllEdges = false
FEATURE [PartDesign::Fillet] Fillet008
  Base = -> Chamfer005 [Edge247,Edge246,Edge245,Edge251,Edge252,Edge253]
  BaseFeature = -> Chamfer005
  Radius = 0.5
  Refine = true
  SupportTransform = false
  Suppressed = false
  UseAllEdges = false
FEATURE [Sketcher::SketchObject] Sketch020
  ArcFitTolerance = 1e-06
  AttachmentSupport = -> [Fillet008]
  ExternalGeometry = -> [Fillet008]
  ExternalTypes = [0]
  FullyConstrained = true
  MakeInternals = false
  MapMode = 5
  Placement = pos=(0,0,2.6498) rot=(1,0,0;3.14159rad)
  _ExternalGeoVersion = 0
  sketch-geometry (10):
    g0: LineSegment StartX=21.551 StartY=-33.5996 StartZ=0 EndX=21.551 EndY=-45.5996 EndZ=0
    g1: LineSegment StartX=21.551 StartY=-45.5996 StartZ=0 EndX=38.1508 EndY=-45.5996 EndZ=0
    g2: LineSegment StartX=35.7508 StartY=-33.5996 StartZ=0 EndX=21.551 EndY=-33.5996 EndZ=0
    g3: LineSegment StartX=35.7508 StartY=-33.5996 StartZ=0 EndX=38.1508 EndY=-35.9996 EndZ=0
    g4: LineSegment StartX=38.1508 StartY=-35.9996 StartZ=0 EndX=38.1508 EndY=-45.5996 EndZ=0
    g5: LineSegment StartX=-44.5492 StartY=-35.9996 StartZ=0 EndX=-42.1491 EndY=-33.5996 EndZ=0
    g6: LineSegment StartX=-42.1491 StartY=-33.5996 StartZ=0 EndX=-27.9492 EndY=-33.5996 EndZ=0
    g7: LineSegment StartX=-27.9492 StartY=-33.5996 StartZ=0 EndX=-27.9492 EndY=-45.5996 EndZ=0
    g8: LineSegment StartX=-27.9492 StartY=-45.5996 StartZ=0 EndX=-44.5492 EndY=-45.5996 EndZ=0
    g9: LineSegment StartX=-44.5492 StartY=-45.5996 StartZ=0 EndX=-44.5492 EndY=-35.9996 EndZ=0
  constraints (23):
    c: Coincident(g0,g1)
    c: Coincident(g2,g0)
    c: Horizontal(g1)
    c: Coincident(g0,g-4)
    c: Coincident(g0,g-4)
    c: Coincident(g3,g2)
    c: Coincident(g3,g-5)
    c: Coincident(g4,g3)
    c: Vertical(g4)
    c: Coincident(g1,g4)
    c: Coincident(g2,g-5)
    c: Coincident(g-8,g5)
    c: PointOnObject(g5,g-8)
    c: Coincident(g5,g6)
    c: Coincident(g6,g-7)
    c: Horizontal(g6)
    c: Coincident(g6,g7)
    c: Coincident(g7,g-7)
    c: Coincident(g7,g8)
    c: Horizontal(g8)
    c: Coincident(g8,g9)
    c: Coincident(g9,g5)
    c: Vertical(g9)
FEATURE [PartDesign::Pocket] Pocket012
  BaseFeature = -> Fillet008
  Direction = (0,0,1)
  Length = 3
  Length2 = 5
  Profile = -> Sketch020
  ReferenceAxis = -> Sketch020 [N_Axis]
  Refine = true
  SideType = 0
  Suppressed = false
  Type = 0
  Type2 = 0
FEATURE [PartDesign::Fillet] Fillet010
  Base = -> Pocket012 [Edge225,Edge220,Edge57,Edge171]
  BaseFeature = -> Pocket012
  Radius = 0.7
  Refine = true
  SupportTransform = false
  Suppressed = false
  UseAllEdges = false
FEATURE [Sketcher::SketchObject] Sketch025
  ArcFitTolerance = 1e-06
  AttachmentSupport = -> [Fillet010]
  ExternalGeometry = -> [Fillet010]
  ExternalTypes = [0]
  FullyConstrained = false
  MakeInternals = false
  MapMode = 5
  Placement = pos=(0,47.1996,0) rot=(0,0.707107,0.707107;3.14159rad)
  _ExternalGeoVersion = 0
  sketch-geometry (6):
    g0: ArcOfCircle CenterX=-29.3095 CenterY=15.6498 CenterZ=0 NormalX=0 NormalY=0 NormalZ=1 AngleXU=0 Radius=1 StartAngle=5.81954 EndAngle=8.96113
    g1: ArcOfCircle CenterX=-38.3095 CenterY=-2.3502 CenterZ=0 NormalX=0 NormalY=0 NormalZ=1 AngleXU=0 Radius=1 StartAngle=2.67795 EndAngle=5.81954
    g2: LineSegment StartX=-28.4151 StartY=15.2026 StartZ=0 EndX=-37.4151 EndY=-2.79741 EndZ=0
    g3: LineSegment StartX=-30.2039 StartY=16.097 StartZ=0 EndX=-39.2039 EndY=-1.90298 EndZ=0
    g4: LineSegment [constr] StartX=-29.3095 StartY=15.6498 StartZ=0 EndX=-29.3095 EndY=18.6498 EndZ=0
    g5: LineSegment [constr] StartX=-38.3095 StartY=-2.3502 StartZ=0 EndX=-38.3095 EndY=-5.3502 EndZ=0
  constraints (15):
    c: Tangent(g0,g2) = 1.5708
    c: Tangent(g0,g3) = -1.5708
    c: Tangent(g1,g2) = 1.5708
    c: Tangent(g1,g3) = -1.5708
    c: Equal(g0,g1)
    c: Radius(g0) = 1
    c: Coincident(g4,g0)
    c: PointOnObject(g4,g-3)
    c: Coincident(g5,g1)
    c: PointOnObject(g5,g-4)
    c: Equal(g4,g5)
    c: Vertical(g5)
    c: Vertical(g4)
    c: DistanceX(g1,g0) = 9
    c: DistanceY(g5,g5) = 3
FEATURE [PartDesign::Pocket] Pocket013
  BaseFeature = -> Fillet010
  Direction = (0,-1,2e-16)
  Length = 1.6
  Length2 = 5
  Profile = -> Sketch025
  ReferenceAxis = -> Sketch025 [N_Axis]
  Refine = true
  SideType = 0
  Suppressed = false
  Type = 0
  Type2 = 0
FEATURE [PartDesign::LinearPattern] LinearPattern
  BaseFeature = -> Pocket013
  Direction = -> Sketch025 [H_Axis]
  Length = 75
  Length2 = 100
  Mode = 0
  Mode2 = 0
  Occurrences = 12
  Occurrences2 = 1
  Offset = 6.81818
  Offset2 = 10
  Originals = -> [Pocket013]
  Refine = true
  Reversed2 = false
  SpacingPattern = [0]
  SpacingPattern2 = [0]
  Spacings = [-1,-1,-1,-1,-1,-1,-1,-1,-1,-1,-1]
  Suppressed = false
  TransformMode = 0
FEATURE [PartDesign::Body] Body001  label="Body"
  AllowCompound = false
  Group = -> [Binder001,Sketch010,Pad003,Sketch011,Pad004,Sketch012,Pocket007,Fillet,Fillet001,Sketch013,Pocket008,Sketch014,Pocket009,Chamfer004,Sketch015,Pad005,Sketch016,Pocket010,Fillet004,Fillet005,Chamfer005,Fillet008,Sketch020,Pocket012,Fillet010,Sketch025,Pocket013,LinearPattern]
  Origin = -> Origin
  Tip = -> LinearPattern
COMPONENT P3 — recipe-attached ("logo-outline", modeled in this document).
Construction recipe (the document's own serialized feature program — sketch geometry with constraints, then the solid features built on it; lengths are millimeters unless a unit is written):

FEATURE [Sketcher::SketchObject] Sketch021
  ArcFitTolerance = 1e-06
  AttachmentOffset = pos=(0,0,-6.35) rot=(0,0,1;0rad)
  AttachmentSupport = -> [XY_Plane062]
  ExternalTypes = [0]
  FullyConstrained = false
  MakeInternals = false
  MapMode = 5
  Placement = pos=(0,0,-6.35) rot=(0,0,1;0rad)
  _ExternalGeoVersion = 0
  sketch-geometry (10):
    g0: LineSegment StartX=16.4753 StartY=20.5288 StartZ=0 EndX=25.4753 EndY=20.5288 EndZ=0
    g1: LineSegment StartX=28.4753 StartY=23.5288 StartZ=0 EndX=28.4753 EndY=32.5288 EndZ=0
    g2: LineSegment StartX=25.4753 StartY=35.5288 StartZ=0 EndX=16.4753 EndY=35.5288 EndZ=0
    g3: LineSegment StartX=13.4753 StartY=32.5288 StartZ=0 EndX=13.4753 EndY=23.5288 EndZ=0
    g4: ArcOfCircle CenterX=16.4753 CenterY=23.5288 CenterZ=0 NormalX=0 NormalY=0 NormalZ=1 AngleXU=0 Radius=3 StartAngle=3.14159 EndAngle=4.71239
    g5: ArcOfCircle CenterX=25.4753 CenterY=23.5288 CenterZ=0 NormalX=0 NormalY=0 NormalZ=1 AngleXU=0 Radius=3 StartAngle=4.71239 EndAngle=6.28319
    g6: ArcOfCircle CenterX=25.4753 CenterY=32.5288 CenterZ=0 NormalX=0 NormalY=0 NormalZ=1 AngleXU=0 Radius=3 StartAngle=0 EndAngle=1.5708
    g7: ArcOfCircle CenterX=16.4753 CenterY=32.5288 CenterZ=0 NormalX=0 NormalY=0 NormalZ=1 AngleXU=0 Radius=3 StartAngle=1.5708 EndAngle=3.14159
    g8: GeomPoint [constr] X=13.4753 Y=20.5288 Z=0
    g9: GeomPoint [constr] X=28.4753 Y=35.5288 Z=0
  constraints (22):
    c: Tangent(g0,g4) = -1.5708
    c: Tangent(g0,g5) = -1.5708
    c: Tangent(g1,g5) = -1.5708
    c: Tangent(g1,g6) = -1.5708
    c: Tangent(g2,g6) = -1.5708
    c: Tangent(g2,g7) = -1.5708
    c: Tangent(g3,g7) = -1.5708
    c: Tangent(g3,g4) = -1.5708
    c: Horizontal(g0)
    c: Horizontal(g2)
    c: Vertical(g1)
    c: Vertical(g3)
    c: Equal(g4,g5)
    c: Equal(g5,g6)
    c: Equal(g6,g7)
    c: PointOnObject(g8,g0)
    c: PointOnObject(g8,g3)
    c: PointOnObject(g9,g1)
    c: PointOnObject(g9,g2)
    c: Distance(g1,g3) = 15
    c: Distance(g0,g2) = 15
    c: Radius(g5) = 3
FEATURE [PartDesign::Pad] Pad008
  Direction = (0,0,1)
  Length = 1
  Length2 = 10
  Profile = -> Sketch021
  ReferenceAxis = -> Sketch021 [N_Axis]
  Refine = true
  Reversed = true
  SideType = 0
  Suppressed = false
  Type = 0
  Type2 = 0
FEATURE [PartDesign::Body] Body002  label="logo-outline"
  AllowCompound = false
  Group = -> [Sketch021,Pad008]
  Origin = -> Origin062
  Tip = -> Pad008
COMPONENT P4 — recipe-attached ("logo-controller", modeled in this document).
Construction recipe (the document's own serialized feature program — sketch geometry with constraints, then the solid features built on it; lengths are millimeters unless a unit is written):

FEATURE [PartDesign::SubShapeBinder] Binder002
  BindCopyOnChange = 0
  BindMode = 0
  ClaimChildren = false
  Context = -> Body003 [Binder002.]
  Fuse = false
  MakeFace = true
  OffsetFill = false
  OffsetIntersection = false
  OffsetJoinType = 0
  OffsetOpenResult = false
  PartialLoad = false
  Refine = true
  Relative = true
  Support = -> [Body002,Sketch022]
  _Version = 2
FEATURE [Sketcher::SketchObject] Sketch022
  ArcFitTolerance = 1e-06
  ExternalTypes = [0]
  FullyConstrained = false
  MakeInternals = false
  Placement = pos=(0,0,-6.35) rot=(0,0,1;0rad)
  _ExternalGeoVersion = 0
  sketch-geometry (18):
    g0: BSplineCurve PolesCount=2 KnotsCount=2 Degree=1 IsPeriodic=0
    g1: BSplineCurve PolesCount=4 KnotsCount=2 Degree=3 IsPeriodic=0
    g2: BSplineCurve PolesCount=4 KnotsCount=2 Degree=3 IsPeriodic=0
    g3: BSplineCurve PolesCount=4 KnotsCount=2 Degree=3 IsPeriodic=0
    g4: BSplineCurve PolesCount=4 KnotsCount=2 Degree=3 IsPeriodic=0
    g5: BSplineCurve PolesCount=4 KnotsCount=2 Degree=3 IsPeriodic=0
    g6: BSplineCurve PolesCount=4 KnotsCount=2 Degree=3 IsPeriodic=0
    g7: BSplineCurve PolesCount=2 KnotsCount=2 Degree=1 IsPeriodic=0
    g8: BSplineCurve PolesCount=2 KnotsCount=2 Degree=1 IsPeriodic=0
    g9: BSplineCurve PolesCount=2 KnotsCount=2 Degree=1 IsPeriodic=0
    g10: BSplineCurve PolesCount=4 KnotsCount=2 Degree=3 IsPeriodic=0
    g11: BSplineCurve PolesCount=4 KnotsCount=2 Degree=3 IsPeriodic=0
    g12: BSplineCurve PolesCount=4 KnotsCount=2 Degree=3 IsPeriodic=0
    g13: BSplineCurve PolesCount=4 KnotsCount=2 Degree=3 IsPeriodic=0
    g14: BSplineCurve PolesCount=2 KnotsCount=2 Degree=1 IsPeriodic=0
    g15: BSplineCurve PolesCount=4 KnotsCount=2 Degree=3 IsPeriodic=0
    g16: BSplineCurve PolesCount=2 KnotsCount=2 Degree=1 IsPeriodic=0
    g17: BSplineCurve PolesCount=2 KnotsCount=2 Degree=1 IsPeriodic=0
  constraints (18):
    c: Coincident(g0,g1)
    c: Coincident(g1,g2)
    c: Coincident(g2,g3)
    c: Coincident(g3,g4)
    c: Coincident(g4,g5)
    c: Coincident(g5,g6)
    c: Coincident(g6,g7)
    c: Coincident(g7,g8)
    c: Coincident(g8,g9)
    c: Coincident(g9,g10)
    c: Coincident(g10,g11)
    c: Coincident(g11,g12)
    c: Coincident(g12,g13)
    c: Coincident(g13,g14)
    c: Coincident(g14,g15)
    c: Coincident(g15,g16)
    c: Coincident(g16,g17)
    c: Coincident(g17,g0)
FEATURE [PartDesign::Pad] Pad009
  Direction = (0,0,1)
  Length = 1
  Length2 = 10
  Placement = pos=(0,0,-6.35) rot=(0,0,1;0rad)
  Profile = -> Sketch022
  ReferenceAxis = -> Sketch022 [N_Axis]
  Refine = true
  Reversed = true
  SideType = 0
  Suppressed = false
  Type = 0
  Type2 = 0
FEATURE [PartDesign::Body] Body003  label="logo-controller"
  AllowCompound = false
  Group = -> [Binder002,Sketch022,Pad009]
  Origin = -> Origin063
  Tip = -> Pad009
COMPONENT P5 — recipe-attached ("logo-led", modeled in this document).
Construction recipe (the document's own serialized feature program — sketch geometry with constraints, then the solid features built on it; lengths are millimeters unless a unit is written):

FEATURE [PartDesign::SubShapeBinder] Binder003
  BindCopyOnChange = 0
  BindMode = 0
  ClaimChildren = false
  Context = -> Body004 [Binder003.]
  Fuse = false
  MakeFace = true
  OffsetFill = false
  OffsetIntersection = false
  OffsetJoinType = 0
  OffsetOpenResult = false
  PartialLoad = false
  Refine = true
  Relative = true
  Support = -> [Body003,Body002]
  _Version = 2
FEATURE [Sketcher::SketchObject] Sketch023
  ArcFitTolerance = 1e-06
  AttachmentSupport = -> [Binder003]
  ExternalGeometry = -> [Binder003]
  ExternalTypes = [0]
  FullyConstrained = false
  MakeInternals = false
  MapMode = 5
  Placement = pos=(0,0,-7.35) rot=(1,0,0;3.14159rad)
  _ExternalGeoVersion = 0
  sketch-geometry (6):
    g0: LineSegment StartX=19.1434 StartY=-28.7844 StartZ=0 EndX=22.8073 EndY=-28.7844 EndZ=0
    g1: LineSegment StartX=22.8073 StartY=-28.7844 StartZ=0 EndX=22.8073 EndY=-32.4468 EndZ=0
    g2: ArcOfCircle CenterX=20.9753 CenterY=-32.4468 CenterZ=0 NormalX=0 NormalY=0 NormalZ=1 AngleXU=0 Radius=1.83197 StartAngle=3.14159 EndAngle=6.28319
    g3: LineSegment StartX=19.1434 StartY=-32.4468 StartZ=0 EndX=19.1434 EndY=-28.7844 EndZ=0
    g4: LineSegment [constr] StartX=19.1434 StartY=-28.7844 StartZ=0 EndX=13.4753 EndY=-28.7844 EndZ=0
    g5: LineSegment [constr] StartX=22.8073 StartY=-28.7844 StartZ=0 EndX=28.4753 EndY=-28.7844 EndZ=0
  constraints (14):
    c: Horizontal(g0)
    c: Coincident(g0,g1)
    c: Vertical(g1)
    c: Tangent(g1,g2) = 1.5708
    c: Tangent(g2,g3) = 1.5708
    c: Coincident(g3,g0)
    c: Horizontal(g2,g1)
    c: Coincident(g4,g0)
    c: PointOnObject(g4,g-3)
    c: Horizontal(g4)
    c: Coincident(g5,g0)
    c: PointOnObject(g5,g-4)
    c: Horizontal(g5)
    c: Equal(g4,g5)
FEATURE [PartDesign::Pad] Pad010
  Direction = (0,0,-1)
  Length = 1
  Length2 = 10
  Profile = -> Sketch023
  ReferenceAxis = -> Sketch023 [N_Axis]
  Refine = true
  Reversed = true
  SideType = 0
  Suppressed = false
  Type = 0
  Type2 = 0
FEATURE [PartDesign::Body] Body004  label="logo-led"
  AllowCompound = false
  Group = -> [Binder003,Sketch023,Pad010]
  Origin = -> Origin064
  Tip = -> Pad010
COMPONENT P6 — recipe-attached ("logo-led-outline", modeled in this document).
Construction recipe (the document's own serialized feature program — sketch geometry with constraints, then the solid features built on it; lengths are millimeters unless a unit is written):

FEATURE [PartDesign::SubShapeBinder] Binder004
  BindCopyOnChange = 0
  BindMode = 0
  ClaimChildren = false
  Context = -> Body005 [Binder004.]
  Fuse = false
  MakeFace = true
  OffsetFill = false
  OffsetIntersection = false
  OffsetJoinType = 0
  OffsetOpenResult = false
  PartialLoad = false
  Refine = true
  Relative = true
  Support = -> [Body004]
  _Version = 2
FEATURE [Sketcher::SketchObject] Sketch026
  ArcFitTolerance = 1e-06
  AttachmentSupport = -> [Binder004]
  ExternalGeometry = -> [Binder004]
  ExternalTypes = [0]
  FullyConstrained = true
  MakeInternals = false
  MapMode = 5
  Placement = pos=(0,0,-6.35) rot=(0,0,1;0rad)
  _ExternalGeoVersion = 0
  sketch-geometry (4):
    g0: LineSegment StartX=18.6434 StartY=32.4468 StartZ=0 EndX=18.6434 EndY=28.2844 EndZ=0
    g1: LineSegment StartX=18.6434 StartY=28.2844 StartZ=0 EndX=23.3073 EndY=28.2844 EndZ=0
    g2: LineSegment StartX=23.3073 StartY=28.2844 StartZ=0 EndX=23.3073 EndY=32.4468 EndZ=0
    g3: ArcOfCircle CenterX=20.9753 CenterY=32.4468 CenterZ=0 NormalX=0 NormalY=0 NormalZ=1 AngleXU=0 Radius=2.33197 StartAngle=0 EndAngle=3.14159
  constraints (11):
    c: Vertical(g0)
    c: Coincident(g0,g1)
    c: Horizontal(g1)
    c: Coincident(g1,g2)
    c: Vertical(g2)
    c: Tangent(g2,g3) = -1.5708
    c: Coincident(g3,g0)
    c: Coincident(g3,g-5)
    c: Distance(g-4,g1) = 0.5
    c: Distance(g-4,g0) = 0.5
    c: Horizontal(g0,g-5)
FEATURE [PartDesign::Pad] Pad011
  Direction = (0,0,1)
  Length = 1
  Length2 = 10
  Profile = -> Sketch026
  ReferenceAxis = -> Sketch026 [N_Axis]
  Refine = true
  Reversed = true
  SideType = 0
  Suppressed = false
  Type = 0
  Type2 = 0
FEATURE [PartDesign::Body] Body005  label="logo-led-outline"
  AllowCompound = false
  Group = -> [Binder004,Sketch026,Pad011]
  Origin = -> Origin065
  Tip = -> Pad011
PROVENANCE & LICENSES
A FreeCAD (.FCStd) document from a public repository crawl; recipes are the document's own serialized feature recipes (and, for linked parts, companion documents' recipes).
License: mit.
